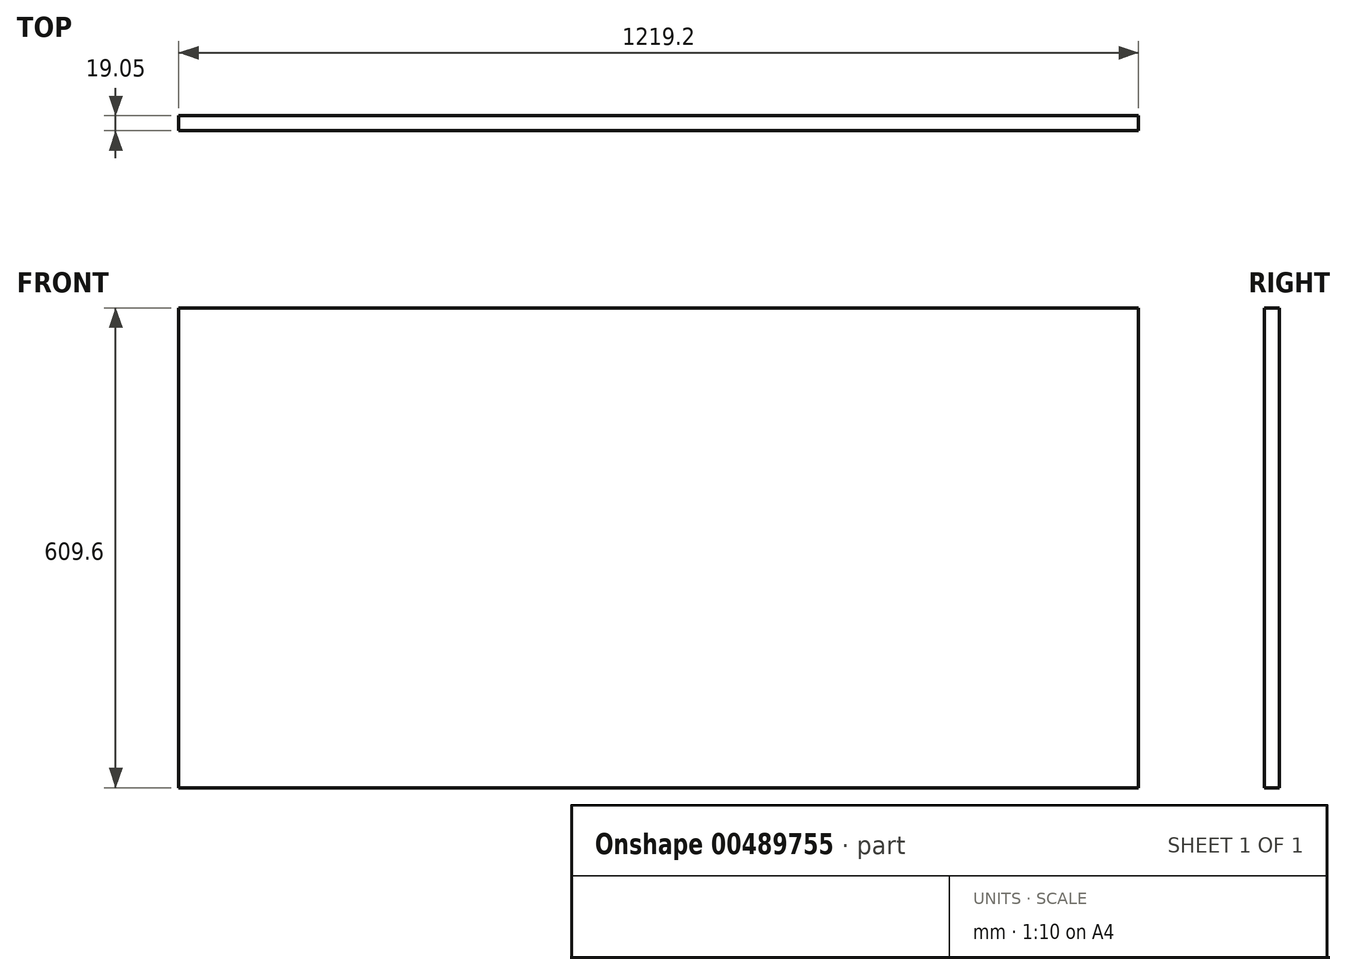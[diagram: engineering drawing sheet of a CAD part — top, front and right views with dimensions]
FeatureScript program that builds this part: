
annotation { "Feature Type Name" : "Feature", "Feature Type Description" : "" }
export const myFeature = defineFeature(function(context is Context, id is Id, definition is map)
    precondition{}
    {
        {
            var Q0;
            Q0=qCreatedBy(makeId("Front.planeOp"),FACE);
            var sketch = newSketch(context, id + "F0", { "sketchPlane" : qUnion([Q0])});
            skLineSegment(sketch, "E0.bottom", {"start": v(612.35, 124.52) * mm, "end": v(-606.85, 124.52) * mm});
            skLineSegment(sketch, "E0.top", {"start": v(612.35, -485.08) * mm, "end": v(-606.85, -485.08) * mm});
            skLineSegment(sketch, "E0.left", {"start": v(612.35, 124.52) * mm, "end": v(612.35, -485.08) * mm});
            skLineSegment(sketch, "E0.right", {"start": v(-606.85, 124.52) * mm, "end": v(-606.85, -485.08) * mm});
            skSolve(sketch);
        }
        {
            var Q0;
            Q0=makeQuery(id+"F0.imprint","IMPRINT",FACE,{"disambiguationData":[TD([[makeQuery(id+"F0.imprint","IMPRINT",EDGE,{"derivedFrom":sQuery(id+"F0.wireOp",EDGE,"E0.bottom")}),1.0]])]});
            extrude(context, id + "F1", {"entities" : qUnion([Q0]), "depth" : 19.05 * mm});
        }
    });
